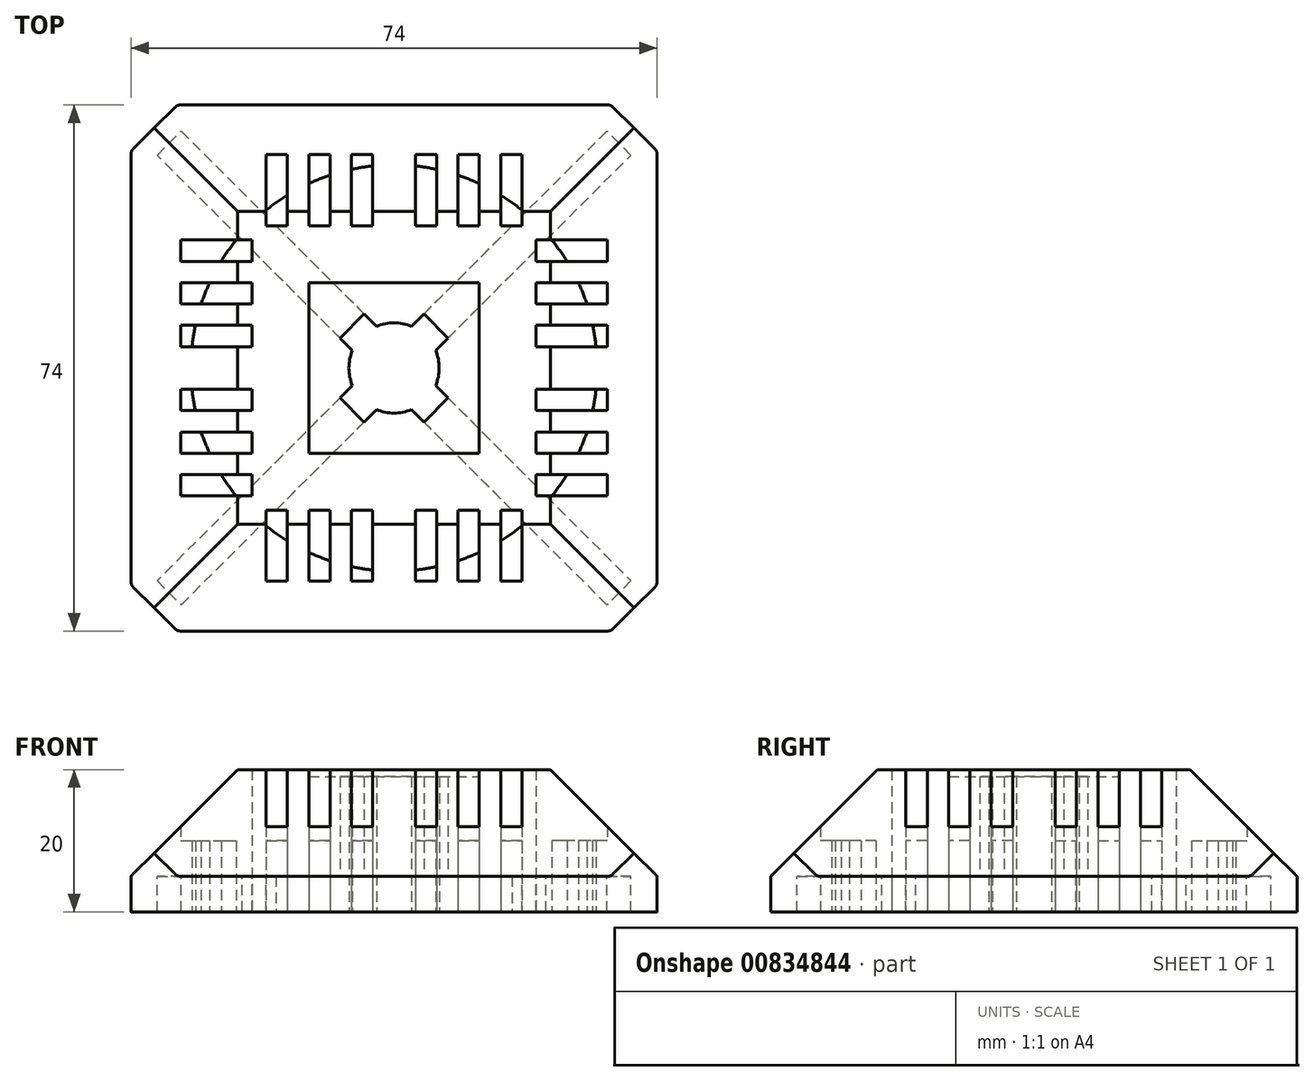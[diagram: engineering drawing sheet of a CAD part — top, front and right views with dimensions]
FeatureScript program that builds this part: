
annotation { "Feature Type Name" : "Feature", "Feature Type Description" : "" }
export const myFeature = defineFeature(function(context is Context, id is Id, definition is map)
    precondition{}
    {
        {
            var Q0;
            Q0=qCreatedBy(makeId("Top.planeOp"),FACE);
            var sketch = newSketch(context, id + "F0", { "sketchPlane" : qUnion([Q0])});
            skLineSegment(sketch, "E0.bottom", {"start": v(0, 0) * mm, "end": v(-37, 0) * mm});
            skLineSegment(sketch, "E0.top", {"start": v(0, 37) * mm, "end": v(-30.5, 37) * mm});
            skLineSegment(sketch, "E0.left", {"start": v(0, 0) * mm, "end": v(0, 37) * mm});
            skLineSegment(sketch, "E0.right", {"start": v(-37, 0) * mm, "end": v(-37, 30.5) * mm});
            skLineSegment(sketch, "E1", {"start": v(-30.5, 37) * mm, "end": v(-37, 30.5) * mm});
            skSolve(sketch);
        }
        {
            var Q0;
            Q0 = qSketchRegion(id + "F0", true);
            extrude(context, id + "F1", {"entities" : qUnion([Q0]), "depth" : 20 * mm, "offsetDistance" : 25 * mm});
        }
        {
            var Q0;
            Q0=makeQuery(id+"F1.opExtrude","CAP_FACE",FACE,{"disambiguationData":[OSD([sQuery(id+"F0.wireOp",EDGE,"E0.bottom"),sQuery(id+"F0.wireOp",EDGE,"E0.top"),sQuery(id+"F0.wireOp",EDGE,"E0.left"),sQuery(id+"F0.wireOp",EDGE,"E0.right"),sQuery(id+"F0.wireOp",EDGE,"E1")])],"isStart":false});
            var sketch = newSketch(context, id + "F2", { "sketchPlane" : qUnion([Q0])});
            skLineSegment(sketch, "E2", {"start": v(-33.75, 33.75) * mm, "end": v(0, 0) * mm, "construction": true});
            skLineSegment(sketch, "E3", {"start": v(-29.93, 33.33) * mm, "end": v(-33.33, 29.93) * mm});
            skLineSegment(sketch, "E4", {"start": v(-33.33, 29.93) * mm, "end": v(-26.6, 23.21) * mm});
            skLineSegment(sketch, "E5", {"start": v(-26.6, 23.21) * mm, "end": v(-23.21, 26.6) * mm});
            skLineSegment(sketch, "E6", {"start": v(-23.21, 26.6) * mm, "end": v(-29.93, 33.33) * mm});
            skPoint(sketch, "E7", {"position": v(-24.91, 24.91) * mm});
            skSolve(sketch);
        }
        {
            var Q0;
            Q0 = qSketchRegion(id + "F2", true);
            var Q1;
            Q1=makeQuery(id+"F1.opExtrude","CAP_FACE",FACE,{"disambiguationData":[OSD([sQuery(id+"F0.wireOp",EDGE,"E0.bottom"),sQuery(id+"F0.wireOp",EDGE,"E0.top"),sQuery(id+"F0.wireOp",EDGE,"E0.left"),sQuery(id+"F0.wireOp",EDGE,"E0.right"),sQuery(id+"F0.wireOp",EDGE,"E1")])],"isStart":true});
            extrude(context, id + "F3", {"entities" : qUnion([Q0]), "operationType" : NewBodyOperationType.REMOVE, "endBound" : BoundingType.UP_TO_SURFACE, "oppositeDirection" : true, "depth" : 25 * mm, "endBoundEntityFace" : qUnion([Q1]), "offsetDistance" : 25 * mm, "hasSecondDirection" : true, "secondDirectionOppositeDirection" : true, "secondDirectionDepth" : 15 * mm});
        }
        {
            var Q0;
            Q0=makeQuery(id+"F1.opExtrude","CAP_FACE",FACE,{"disambiguationData":[OSD([sQuery(id+"F0.wireOp",EDGE,"E0.bottom"),sQuery(id+"F0.wireOp",EDGE,"E0.top"),sQuery(id+"F0.wireOp",EDGE,"E0.left"),sQuery(id+"F0.wireOp",EDGE,"E0.right"),sQuery(id+"F0.wireOp",EDGE,"E1")])],"isStart":true});
            var sketch = newSketch(context, id + "F4", { "sketchPlane" : qUnion([Q0])});
            skCircle(sketch, "E8", {"center": v(0, 0) * mm, "radius": 6.35 * mm});
            skSolve(sketch);
        }
        {
            var Q0;
            Q0 = qSketchRegion(id + "F4", true);
            var Q1;
            Q1=makeQuery(id+"F1.opExtrude","CAP_FACE",FACE,{"disambiguationData":[OSD([sQuery(id+"F0.wireOp",EDGE,"E0.bottom"),sQuery(id+"F0.wireOp",EDGE,"E0.top"),sQuery(id+"F0.wireOp",EDGE,"E0.left"),sQuery(id+"F0.wireOp",EDGE,"E0.right"),sQuery(id+"F0.wireOp",EDGE,"E1")])],"isStart":false});
            extrude(context, id + "F5", {"entities" : qUnion([Q0]), "operationType" : NewBodyOperationType.REMOVE, "endBound" : BoundingType.UP_TO_SURFACE, "oppositeDirection" : true, "depth" : 15 * mm, "endBoundEntityFace" : qUnion([Q1]), "offsetDistance" : 25 * mm});
        }
        {
            var Q0;
            Q0=makeQuery(id+"F1.opExtrude","SWEPT_FACE",FACE,{"disambiguationData":[OSD([sQuery(id+"F0.wireOp",EDGE,"E0.bottom")])]});
            var sketch = newSketch(context, id + "F6", { "sketchPlane" : qUnion([Q0])});
            skLineSegment(sketch, "E9", {"start": v(-37, 20) * mm, "end": v(-37, 5) * mm});
            skLineSegment(sketch, "E10", {"start": v(-37, 5) * mm, "end": v(-22, 20) * mm});
            skLineSegment(sketch, "E11", {"start": v(-22, 20) * mm, "end": v(-37, 20) * mm});
            skSolve(sketch);
        }
        {
            var Q0;
            Q0 = qSketchRegion(id + "F6", true);
            var Q1;
            Q1=makeQuery(id+"F1.opExtrude","SWEPT_FACE",FACE,{"disambiguationData":[OSD([sQuery(id+"F0.wireOp",EDGE,"E0.top")])]});
            extrude(context, id + "F7", {"entities" : qUnion([Q0]), "operationType" : NewBodyOperationType.REMOVE, "endBound" : BoundingType.UP_TO_SURFACE, "oppositeDirection" : true, "depth" : 25 * mm, "endBoundEntityFace" : qUnion([Q1]), "offsetDistance" : 25 * mm});
        }
        {
            var Q0;
            Q0=makeQuery(id+"F1.opExtrude","SWEPT_FACE",FACE,{"disambiguationData":[OSD([sQuery(id+"F0.wireOp",EDGE,"E0.left")])]});
            var sketch = newSketch(context, id + "F8", { "sketchPlane" : qUnion([Q0])});
            skLineSegment(sketch, "E12", {"start": v(22, 20) * mm, "end": v(37, 20) * mm});
            skLineSegment(sketch, "E13", {"start": v(37, 20) * mm, "end": v(37, 5) * mm});
            skLineSegment(sketch, "E14", {"start": v(37, 5) * mm, "end": v(22, 20) * mm});
            skSolve(sketch);
        }
        {
            var Q0;
            Q0 = qSketchRegion(id + "F8", true);
            var Q1;
            Q1=makeQuery(id+"F1.opExtrude","SWEPT_FACE",FACE,{"disambiguationData":[OSD([sQuery(id+"F0.wireOp",EDGE,"E0.right")])]});
            extrude(context, id + "F9", {"entities" : qUnion([Q0]), "operationType" : NewBodyOperationType.REMOVE, "endBound" : BoundingType.UP_TO_SURFACE, "oppositeDirection" : true, "depth" : 25 * mm, "endBoundEntityFace" : qUnion([Q1]), "offsetDistance" : 25 * mm});
        }
        {
            var Q0;
            Q0=makeQuery(id+"F0dVvwK0POYM6dp_1.boolean.opBoolean","MERGE",FACE,{"derivedFrom":[makeQuery(id+"F1.opExtrude","CAP_FACE",FACE,{"disambiguationData":[OSD([sQuery(id+"F0.wireOp",EDGE,"E0.bottom"),sQuery(id+"F0.wireOp",EDGE,"E0.top"),sQuery(id+"F0.wireOp",EDGE,"E0.left"),sQuery(id+"F0.wireOp",EDGE,"E0.right"),sQuery(id+"F0.wireOp",EDGE,"E1")])],"isStart":true}),makeQuery(id+"F0dVvwK0POYM6dp_1.opExtrude","CAP_FACE",FACE,{"disambiguationData":[OSD([sQuery(id+"FMhlsUE3KlxPvWO_1.wireOp",EDGE,"a645a824-875d-4bab-b828-a21e6561569e.0"),sQuery(id+"FMhlsUE3KlxPvWO_1.wireOp",EDGE,"a645a824-875d-4bab-b828-a21e6561569e.1"),sQuery(id+"FMhlsUE3KlxPvWO_1.wireOp",EDGE,"a645a824-875d-4bab-b828-a21e6561569e.2"),sQuery(id+"FMhlsUE3KlxPvWO_1.wireOp",EDGE,"sNXyJJYW-g3ji-6H4r-cV3o-3Jo7wu7bBI5y"),sQuery(id+"FMhlsUE3KlxPvWO_1.wireOp",EDGE,"TGwURDNx-GOZI-plmj-YHV4-LnZpdH2vIoyB"),sQuery(id+"FMhlsUE3KlxPvWO_1.wireOp",EDGE,"Hqw0AfeI-sJu5-bhwd-Blhz-vAiwjAEWYiLs"),sQuery(id+"FMhlsUE3KlxPvWO_1.wireOp",EDGE,"2klhEoJP-fmrM-WXoO-Dq7c-Udh8YoXaK1c8"),sQuery(id+"FMhlsUE3KlxPvWO_1.wireOp",EDGE,"adSKBLk1-AzaB-Y6pe-8Uw0-vup0GxfDr6Yb")])],"isStart":true})]});
            var sketch = newSketch(context, id + "F10", { "sketchPlane" : qUnion([Q0])});
            skLineSegment(sketch, "E15.bottom", {"start": v(-30, -3) * mm, "end": v(-20, -3) * mm});
            skLineSegment(sketch, "E15.top", {"start": v(-30, -6) * mm, "end": v(-20, -6) * mm});
            skLineSegment(sketch, "E15.left", {"start": v(-30, -3) * mm, "end": v(-30, -6) * mm});
            skLineSegment(sketch, "E15.right", {"start": v(-20, -3) * mm, "end": v(-20, -6) * mm});
            skLineSegment(sketch, "E16.bottom", {"start": v(-3, -20) * mm, "end": v(-6, -20) * mm});
            skLineSegment(sketch, "E16.top", {"start": v(-3, -30) * mm, "end": v(-6, -30) * mm});
            skLineSegment(sketch, "E16.left", {"start": v(-3, -20) * mm, "end": v(-3, -30) * mm});
            skLineSegment(sketch, "E16.right", {"start": v(-6, -20) * mm, "end": v(-6, -30) * mm});
            skLineSegment(sketch, "E17.bottom", {"start": v(-30, -9) * mm, "end": v(-20, -9) * mm});
            skLineSegment(sketch, "E17.top", {"start": v(-30, -12) * mm, "end": v(-20, -12) * mm});
            skLineSegment(sketch, "E17.left", {"start": v(-30, -9) * mm, "end": v(-30, -12) * mm});
            skLineSegment(sketch, "E17.right", {"start": v(-20, -9) * mm, "end": v(-20, -12) * mm});
            skLineSegment(sketch, "E18.bottom", {"start": v(-30, -15) * mm, "end": v(-20, -15) * mm});
            skLineSegment(sketch, "E18.top", {"start": v(-30, -18) * mm, "end": v(-20, -18) * mm});
            skLineSegment(sketch, "E18.left", {"start": v(-30, -15) * mm, "end": v(-30, -18) * mm});
            skLineSegment(sketch, "E18.right", {"start": v(-20, -15) * mm, "end": v(-20, -18) * mm});
            skLineSegment(sketch, "E19.bottom", {"start": v(-9, -20) * mm, "end": v(-12, -20) * mm});
            skLineSegment(sketch, "E19.top", {"start": v(-9, -30) * mm, "end": v(-12, -30) * mm});
            skLineSegment(sketch, "E19.left", {"start": v(-9, -20) * mm, "end": v(-9, -30) * mm});
            skLineSegment(sketch, "E19.right", {"start": v(-12, -20) * mm, "end": v(-12, -30) * mm});
            skLineSegment(sketch, "E20.bottom", {"start": v(-15, -20) * mm, "end": v(-18, -20) * mm});
            skLineSegment(sketch, "E20.top", {"start": v(-15, -30) * mm, "end": v(-18, -30) * mm});
            skLineSegment(sketch, "E20.left", {"start": v(-15, -20) * mm, "end": v(-15, -30) * mm});
            skLineSegment(sketch, "E20.right", {"start": v(-18, -20) * mm, "end": v(-18, -30) * mm});
            skSolve(sketch);
        }
        {
            var Q0;
            Q0 = qSketchRegion(id + "F10", true);
            var Q1;
            Q1=makeQuery(id+"F1.opExtrude","CAP_FACE",FACE,{"disambiguationData":[OSD([sQuery(id+"F0.wireOp",EDGE,"E0.bottom"),sQuery(id+"F0.wireOp",EDGE,"E0.top"),sQuery(id+"F0.wireOp",EDGE,"E0.left"),sQuery(id+"F0.wireOp",EDGE,"E0.right"),sQuery(id+"F0.wireOp",EDGE,"E1")])],"isStart":false});
            extrude(context, id + "F11", {"entities" : qUnion([Q0]), "operationType" : NewBodyOperationType.REMOVE, "endBound" : BoundingType.UP_TO_SURFACE, "oppositeDirection" : true, "depth" : 25 * mm, "endBoundEntityFace" : qUnion([Q1]), "offsetDistance" : 25 * mm});
        }
        {
            var Q0;
            Q0=makeQuery(id+"F3.boolean.opBoolean","COPY",FACE,{"derivedFrom":makeQuery(id+"F3.opExtrude","SWEPT_FACE",FACE,{"disambiguationData":[OSD([sQuery(id+"F2.wireOp",EDGE,"E5")])]})});
            extrude(context, id + "F12", {"entities" : qUnion([Q0]), "operationType" : NewBodyOperationType.REMOVE, "oppositeDirection" : true, "depth" : 32 * mm, "offsetDistance" : 25 * mm});
        }
        {
            var Q0;
            {var subQ0=sQuery(id+"F2.wireOp",EDGE,"E5");Q0=makeQuery(id+"F12.boolean.opBoolean","MERGE",FACE,{"derivedFrom":[makeQuery(id+"F3.boolean.opBoolean","COPY",FACE,{"derivedFrom":makeQuery(id+"F3.opExtrude","CAP_FACE",FACE,{"disambiguationData":[OSD([sQuery(id+"F2.wireOp",EDGE,"E3"),sQuery(id+"F2.wireOp",EDGE,"E4"),subQ0,sQuery(id+"F2.wireOp",EDGE,"E6")])],"isStart":true})})],"fromTools":[makeQuery(id+"F12.opExtrude","SWEPT_FACE",FACE,{"disambiguationData":[OSD([subQ0]),TDD([makeQuery(id+"F3.boolean.opBoolean","COPY",EDGE,{"derivedFrom":makeQuery(id+"F3.opExtrude","CAP_EDGE",EDGE,{"disambiguationData":[OSD([subQ0])],"isStart":true})})])]})]});}
            var sketch = newSketch(context, id + "F13", { "sketchPlane" : qUnion([Q0])});
            skLineSegment(sketch, "E21", {"start": v(-7.6, -4.2) * mm, "end": v(-5.48, -2.09) * mm});
            skLineSegment(sketch, "E22", {"start": v(-5.48, -2.09) * mm, "end": v(-2.09, -5.48) * mm});
            skLineSegment(sketch, "E23", {"start": v(-2.09, -5.48) * mm, "end": v(-4.2, -7.6) * mm});
            skLineSegment(sketch, "E24", {"start": v(-4.2, -7.6) * mm, "end": v(-7.6, -4.2) * mm});
            skSolve(sketch);
        }
        {
            var Q0;
            Q0 = qSketchRegion(id + "F13", true);
            var Q1;
            Q1=makeQuery(id+"F1.opExtrude","CAP_FACE",FACE,{"disambiguationData":[OSD([sQuery(id+"F0.wireOp",EDGE,"E0.bottom"),sQuery(id+"F0.wireOp",EDGE,"E0.top"),sQuery(id+"F0.wireOp",EDGE,"E0.left"),sQuery(id+"F0.wireOp",EDGE,"E0.right"),sQuery(id+"F0.wireOp",EDGE,"E1")])],"isStart":false});
            extrude(context, id + "F14", {"entities" : qUnion([Q0]), "operationType" : NewBodyOperationType.REMOVE, "endBound" : BoundingType.UP_TO_SURFACE, "oppositeDirection" : true, "depth" : 5 * mm, "endBoundEntityFace" : qUnion([Q1]), "offsetDistance" : 25 * mm});
        }
        {
            var Q0;
            Q0=makeQuery(id+"F1.opExtrude","CAP_FACE",FACE,{"disambiguationData":[OSD([sQuery(id+"F0.wireOp",EDGE,"E0.bottom"),sQuery(id+"F0.wireOp",EDGE,"E0.top"),sQuery(id+"F0.wireOp",EDGE,"E0.left"),sQuery(id+"F0.wireOp",EDGE,"E0.right"),sQuery(id+"F0.wireOp",EDGE,"E1")])],"isStart":false});
            var sketch = newSketch(context, id + "F15", { "sketchPlane" : qUnion([Q0])});
            skLineSegment(sketch, "E25.bottom", {"start": v(-12, 0) * mm, "end": v(0, 0) * mm});
            skLineSegment(sketch, "E25.top", {"start": v(-12, 12) * mm, "end": v(0, 12) * mm});
            skLineSegment(sketch, "E25.left", {"start": v(-12, 0) * mm, "end": v(-12, 12) * mm});
            skLineSegment(sketch, "E25.right", {"start": v(0, 0) * mm, "end": v(0, 12) * mm});
            skSolve(sketch);
        }
        {
            var Q0;
            Q0 = qSketchRegion(id + "F15", true);
            extrude(context, id + "F16", {"entities" : qUnion([Q0]), "operationType" : NewBodyOperationType.REMOVE, "oppositeDirection" : true, "depth" : 1 * mm, "offsetDistance" : 25 * mm});
        }
        {
            var Q0;
            Q0=makeQuery(id+"F0dVvwK0POYM6dp_1.boolean.opBoolean","MERGE",FACE,{"derivedFrom":[makeQuery(id+"F1.opExtrude","CAP_FACE",FACE,{"disambiguationData":[OSD([sQuery(id+"F0.wireOp",EDGE,"E0.bottom"),sQuery(id+"F0.wireOp",EDGE,"E0.top"),sQuery(id+"F0.wireOp",EDGE,"E0.left"),sQuery(id+"F0.wireOp",EDGE,"E0.right"),sQuery(id+"F0.wireOp",EDGE,"E1")])],"isStart":true}),makeQuery(id+"F0dVvwK0POYM6dp_1.opExtrude","CAP_FACE",FACE,{"disambiguationData":[OSD([sQuery(id+"FMhlsUE3KlxPvWO_1.wireOp",EDGE,"a645a824-875d-4bab-b828-a21e6561569e.0"),sQuery(id+"FMhlsUE3KlxPvWO_1.wireOp",EDGE,"a645a824-875d-4bab-b828-a21e6561569e.1"),sQuery(id+"FMhlsUE3KlxPvWO_1.wireOp",EDGE,"a645a824-875d-4bab-b828-a21e6561569e.2"),sQuery(id+"FMhlsUE3KlxPvWO_1.wireOp",EDGE,"sNXyJJYW-g3ji-6H4r-cV3o-3Jo7wu7bBI5y"),sQuery(id+"FMhlsUE3KlxPvWO_1.wireOp",EDGE,"TGwURDNx-GOZI-plmj-YHV4-LnZpdH2vIoyB"),sQuery(id+"FMhlsUE3KlxPvWO_1.wireOp",EDGE,"Hqw0AfeI-sJu5-bhwd-Blhz-vAiwjAEWYiLs"),sQuery(id+"FMhlsUE3KlxPvWO_1.wireOp",EDGE,"2klhEoJP-fmrM-WXoO-Dq7c-Udh8YoXaK1c8"),sQuery(id+"FMhlsUE3KlxPvWO_1.wireOp",EDGE,"adSKBLk1-AzaB-Y6pe-8Uw0-vup0GxfDr6Yb")])],"isStart":true})]});
            var sketch = newSketch(context, id + "F17", { "sketchPlane" : qUnion([Q0])});
            skArc(sketch, "E26", {"start": v(-28.42, -3) * mm, "mid": v(-28.22, -4.5) * mm, "end": v(-27.94, -6) * mm});
            skLineSegment(sketch, "E27.bottom", {"start": v(-30, -3) * mm, "end": v(-28.42, -3) * mm});
            skLineSegment(sketch, "E27.top", {"start": v(-30, -6) * mm, "end": v(-27.94, -6) * mm});
            skLineSegment(sketch, "E27.left", {"start": v(-30, -3) * mm, "end": v(-30, -6) * mm});
            skLineSegment(sketch, "E28.bottom", {"start": v(-30, -9) * mm, "end": v(-27.12, -9) * mm});
            skLineSegment(sketch, "E28.top", {"start": v(-30, -12) * mm, "end": v(-25.93, -12) * mm});
            skLineSegment(sketch, "E28.left", {"start": v(-30, -9) * mm, "end": v(-30, -12) * mm});
            skLineSegment(sketch, "E29.bottom", {"start": v(-30, -15) * mm, "end": v(-24.32, -15) * mm});
            skLineSegment(sketch, "E29.top", {"start": v(-30, -18) * mm, "end": v(-22.2, -18) * mm});
            skLineSegment(sketch, "E29.left", {"start": v(-30, -15) * mm, "end": v(-30, -18) * mm});
            skLineSegment(sketch, "E30.bottom", {"start": v(-15, -30) * mm, "end": v(-18, -30) * mm});
            skLineSegment(sketch, "E30.left", {"start": v(-15, -30) * mm, "end": v(-15, -24.32) * mm});
            skLineSegment(sketch, "E30.right", {"start": v(-18, -30) * mm, "end": v(-18, -22.2) * mm});
            skLineSegment(sketch, "E31.bottom", {"start": v(-9, -30) * mm, "end": v(-12, -30) * mm});
            skLineSegment(sketch, "E31.left", {"start": v(-9, -30) * mm, "end": v(-9, -27.12) * mm});
            skLineSegment(sketch, "E31.right", {"start": v(-12, -30) * mm, "end": v(-12, -25.93) * mm});
            skLineSegment(sketch, "E32.bottom", {"start": v(-3, -30) * mm, "end": v(-6, -30) * mm});
            skLineSegment(sketch, "E32.left", {"start": v(-3, -30) * mm, "end": v(-3, -28.42) * mm});
            skLineSegment(sketch, "E32.right", {"start": v(-6, -30) * mm, "end": v(-6, -27.94) * mm});
            skArc(sketch, "E33.trimOffspring", {"start": v(-27.12, -9) * mm, "mid": v(-26.57, -10.52) * mm, "end": v(-25.93, -12) * mm});
            skArc(sketch, "E34.trimOffspring", {"start": v(-24.32, -15) * mm, "mid": v(-23.3, -16.53) * mm, "end": v(-22.2, -18) * mm});
            skPoint(sketch, "E35.orphan", {"position": v(-20, -18) * mm});
            skArc(sketch, "E36.trimOffspring", {"start": v(-18, -22.2) * mm, "mid": v(-16.53, -23.3) * mm, "end": v(-15, -24.32) * mm});
            skPoint(sketch, "E30.top.end.orphan", {"position": v(-18, -20) * mm});
            skArc(sketch, "E37.trimOffspring", {"start": v(-12, -25.93) * mm, "mid": v(-10.52, -26.57) * mm, "end": v(-9, -27.12) * mm});
            skArc(sketch, "E38.trimOffspring", {"start": v(-6, -27.94) * mm, "mid": v(-4.5, -28.22) * mm, "end": v(-3, -28.42) * mm});
            skSolve(sketch);
        }
        {
            var Q0;
            Q0 = qSketchRegion(id + "F17", true);
            extrude(context, id + "F18", {"entities" : qUnion([Q0]), "operationType" : NewBodyOperationType.ADD, "oppositeDirection" : true, "depth" : 10 * mm, "offsetDistance" : 25 * mm});
        }
        {
            var Q0;
            Q0=makeQuery(id+"F1.opExtrude","SWEPT_EDGE",EDGE,{"disambiguationData":[OSD([sQuery(id+"F0.wireOp",EDGE,"E0.right"),sQuery(id+"F0.wireOp",EDGE,"E1")])]});
            var Q1;
            Q1=makeQuery(id+"F1.opExtrude","SWEPT_EDGE",EDGE,{"disambiguationData":[OSD([sQuery(id+"F0.wireOp",EDGE,"E0.top"),sQuery(id+"F0.wireOp",EDGE,"E1")])]});
            fillet(context, id + "F19", {"entities" : qUnion([Q0, Q1]), "tangentPropagation" : true, "radius" : 1 * mm, "defaultsChanged" : false, "vertexSettings" : [], "allowEdgeOverflow" : false});
        }
        {
            var Q0;
            Q0=makeQuery(id+"F1.opExtrude","SWEPT_BODY",BODY,{"disambiguationData":[OSD([sQuery(id+"F0.wireOp",EDGE,"ea2b644c-847e-4850-b3c1-09707df0f97b"),sQuery(id+"F0.wireOp",EDGE,"E0.bottom"),sQuery(id+"F0.wireOp",EDGE,"E0.top"),sQuery(id+"F0.wireOp",EDGE,"E0.left"),sQuery(id+"F0.wireOp",EDGE,"E0.right"),sQuery(id+"F0.wireOp",EDGE,"E1")])]});
            var Q1;
            Q1=qCreatedBy(makeId("Front.planeOp"),FACE);
            mirror(context, id + "F20", {"operationType" : NewBodyOperationType.ADD, "entities" : qUnion([Q0]), "mirrorPlane" : qUnion([Q1])});
        }
        {
            var Q0;
            Q0=makeQuery(id+"F1.opExtrude","SWEPT_BODY",BODY,{"disambiguationData":[OSD([sQuery(id+"F0.wireOp",EDGE,"ea2b644c-847e-4850-b3c1-09707df0f97b"),sQuery(id+"F0.wireOp",EDGE,"E0.bottom"),sQuery(id+"F0.wireOp",EDGE,"E0.top"),sQuery(id+"F0.wireOp",EDGE,"E0.left"),sQuery(id+"F0.wireOp",EDGE,"E0.right"),sQuery(id+"F0.wireOp",EDGE,"E1")])]});
            var Q1;
            Q1=qCreatedBy(makeId("Right.planeOp"),FACE);
            mirror(context, id + "F21", {"operationType" : NewBodyOperationType.ADD, "entities" : qUnion([Q0]), "mirrorPlane" : qUnion([Q1])});
        }
    });
